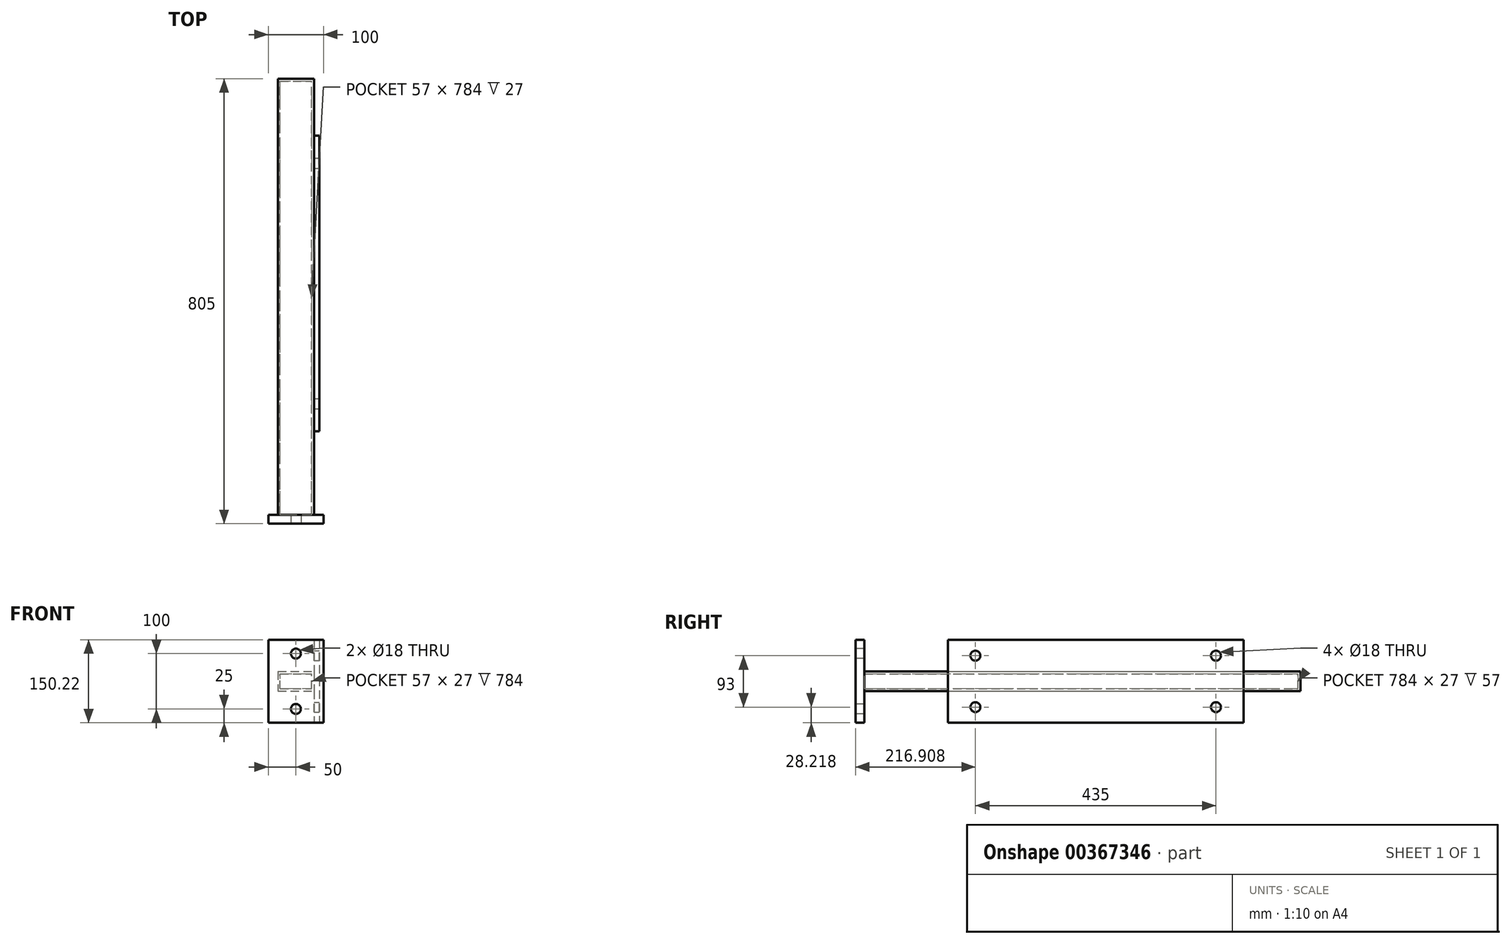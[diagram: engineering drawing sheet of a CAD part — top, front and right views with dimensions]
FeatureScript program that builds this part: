
annotation { "Feature Type Name" : "Feature", "Feature Type Description" : "" }
export const myFeature = defineFeature(function(context is Context, id is Id, definition is map)
    precondition{}
    {
        {
            var Q0;
            Q0=qCreatedBy(makeId("Front.planeOp"),FACE);
            var sketch = newSketch(context, id + "F0", { "sketchPlane" : qUnion([Q0])});
            skLineSegment(sketch, "E0.bottom", {"start": v(-32.5, 17.5) * mm, "end": v(32.5, 17.5) * mm});
            skLineSegment(sketch, "E0.top", {"start": v(-32.5, -17.5) * mm, "end": v(32.5, -17.5) * mm});
            skLineSegment(sketch, "E0.left", {"start": v(-32.5, 17.5) * mm, "end": v(-32.5, -17.5) * mm});
            skLineSegment(sketch, "E0.right", {"start": v(32.5, 17.5) * mm, "end": v(32.5, -17.5) * mm});
            skPoint(sketch, "E0.middle", {"position": v(0, 0) * mm});
            skLineSegment(sketch, "E1.bottom", {"start": v(-28.5, -13.5) * mm, "end": v(28.5, -13.5) * mm});
            skLineSegment(sketch, "E1.top", {"start": v(-28.5, 13.5) * mm, "end": v(28.5, 13.5) * mm});
            skLineSegment(sketch, "E1.left", {"start": v(-28.5, -13.5) * mm, "end": v(-28.5, 13.5) * mm});
            skLineSegment(sketch, "E1.right", {"start": v(28.5, -13.5) * mm, "end": v(28.5, 13.5) * mm});
            skSolve(sketch);
        }
        {
            var Q0;
            Q0 = qSketchRegion(id + "F0", true);
            extrude(context, id + "F1", {"entities" : qUnion([Q0]), "depth" : 784 * mm});
        }
        {
            var Q0;
            Q0=makeQuery(id+"F1.opExtrude","CAP_FACE",FACE,{"disambiguationData":[OSD([sQuery(id+"F0.wireOp",EDGE,"E0.bottom"),sQuery(id+"F0.wireOp",EDGE,"E0.top"),sQuery(id+"F0.wireOp",EDGE,"E0.left"),sQuery(id+"F0.wireOp",EDGE,"E0.right"),sQuery(id+"F0.wireOp",EDGE,"E1.bottom"),sQuery(id+"F0.wireOp",EDGE,"E1.top"),sQuery(id+"F0.wireOp",EDGE,"E1.left"),sQuery(id+"F0.wireOp",EDGE,"E1.right")])],"isStart":false});
            var sketch = newSketch(context, id + "F2", { "sketchPlane" : qUnion([Q0])});
            skLineSegment(sketch, "E2.bottom", {"start": v(-50, -75) * mm, "end": v(50, -75) * mm});
            skLineSegment(sketch, "E2.top", {"start": v(-50, 75) * mm, "end": v(50, 75) * mm});
            skLineSegment(sketch, "E2.left", {"start": v(-50, -75) * mm, "end": v(-50, 75) * mm});
            skLineSegment(sketch, "E2.right", {"start": v(50, -75) * mm, "end": v(50, 75) * mm});
            skPoint(sketch, "E2.middle", {"position": v(0, 0) * mm});
            skSolve(sketch);
        }
        {
            var Q0;
            Q0 = qSketchRegion(id + "F2", true);
            extrude(context, id + "F3", {"entities" : qUnion([Q0]), "operationType" : NewBodyOperationType.ADD, "depth" : 16 * mm});
        }
        {
            var Q0;
            Q0=makeQuery(id+"F3.opExtrude","CAP_FACE",FACE,{"disambiguationData":[OSD([sQuery(id+"F2.wireOp",EDGE,"E2.bottom"),sQuery(id+"F2.wireOp",EDGE,"E2.top"),sQuery(id+"F2.wireOp",EDGE,"E2.left"),sQuery(id+"F2.wireOp",EDGE,"E2.right")])],"isStart":false});
            var sketch = newSketch(context, id + "F4", { "sketchPlane" : qUnion([Q0])});
            skLineSegment(sketch, "E3", {"start": v(0, 75) * mm, "end": v(0, 50) * mm});
            skPoint(sketch, "E3.endSnap0", {"position": v(0, 75) * mm});
            skLineSegment(sketch, "E4", {"start": v(0, -75) * mm, "end": v(0, -50) * mm});
            skPoint(sketch, "E4.endSnap0", {"position": v(0, -75) * mm});
            skSolve(sketch);
        }
        {
            var Q0;
            Q0=sQuery(id+"F4.wireOp",VERTEX,"E3.end");
            var Q1;
            Q1=sQuery(id+"F4.wireOp",VERTEX,"E4.end");
            var Q2;
            Q2=makeQuery(id+"F1.opExtrude","SWEPT_BODY",BODY,{"disambiguationData":[OSD([sQuery(id+"F0.wireOp",EDGE,"E0.bottom"),sQuery(id+"F0.wireOp",EDGE,"E0.top"),sQuery(id+"F0.wireOp",EDGE,"E0.left"),sQuery(id+"F0.wireOp",EDGE,"E0.right"),sQuery(id+"F0.wireOp",EDGE,"E1.bottom"),sQuery(id+"F0.wireOp",EDGE,"E1.top"),sQuery(id+"F0.wireOp",EDGE,"E1.left"),sQuery(id+"F0.wireOp",EDGE,"E1.right")])]});
            hole(context, id + "F5", {"style" : HoleStyle.SIMPLE, "endStyle" : HoleEndStyle.THROUGH, "holeDiameter" : 18 * mm, "isTappedThrough" : true, "tappedDepth" : 12 * mm, "tapClearance" : 3, "locations" : qUnion([Q0, Q1]), "scope" : qUnion([Q2])});
        }
        {
            var Q0;
            Q0=makeQuery(id+"F1.opExtrude","SWEPT_FACE",FACE,{"disambiguationData":[OSD([sQuery(id+"F0.wireOp",EDGE,"E0.right")])]});
            var sketch = newSketch(context, id + "F6", { "sketchPlane" : qUnion([Q0])});
            skLineSegment(sketch, "E5.bottom", {"start": v(-633.1, 75.22) * mm, "end": v(-98.1, 75.22) * mm});
            skLineSegment(sketch, "E5.top", {"start": v(-633.1, -74.78) * mm, "end": v(-98.1, -74.78) * mm});
            skLineSegment(sketch, "E5.left", {"start": v(-633.1, 75.22) * mm, "end": v(-633.1, -74.78) * mm});
            skLineSegment(sketch, "E5.right", {"start": v(-98.1, 75.22) * mm, "end": v(-98.1, -74.78) * mm});
            skSolve(sketch);
        }
        {
            var Q0;
            Q0 = qSketchRegion(id + "F6", true);
            extrude(context, id + "F7", {"entities" : qUnion([Q0]), "operationType" : NewBodyOperationType.ADD, "depth" : 10 * mm});
        }
        {
            var Q0;
            Q0=makeQuery(id+"F7.opExtrude","CAP_FACE",FACE,{"disambiguationData":[OSD([sQuery(id+"F6.wireOp",EDGE,"E5.bottom"),sQuery(id+"F6.wireOp",EDGE,"E5.top"),sQuery(id+"F6.wireOp",EDGE,"E5.left"),sQuery(id+"F6.wireOp",EDGE,"E5.right")])],"isStart":false});
            var sketch = newSketch(context, id + "F8", { "sketchPlane" : qUnion([Q0])});
            skLineSegment(sketch, "E6", {"start": v(-98.1, 75.22) * mm, "end": v(-98.1, 46.22) * mm});
            skLineSegment(sketch, "E7", {"start": v(-98.1, 46.22) * mm, "end": v(-148.1, 46.22) * mm});
            skLineSegment(sketch, "E8", {"start": v(-148.1, 46.22) * mm, "end": v(-148.1, -46.78) * mm});
            skLineSegment(sketch, "E9", {"start": v(-148.1, -46.78) * mm, "end": v(-583.1, -46.78) * mm});
            skLineSegment(sketch, "E10", {"start": v(-583.1, -46.78) * mm, "end": v(-583.1, 46.22) * mm});
            skSolve(sketch);
        }
        {
            var Q0;
            Q0=sQuery(id+"F8.wireOp",VERTEX,"E7.end");
            var Q1;
            Q1=sQuery(id+"F8.wireOp",VERTEX,"E9.start");
            var Q2;
            Q2=sQuery(id+"F8.wireOp",VERTEX,"E10.start");
            var Q3;
            Q3=sQuery(id+"F8.wireOp",VERTEX,"E10.end");
            var Q4;
            Q4=makeQuery(id+"F1.opExtrude","SWEPT_BODY",BODY,{"disambiguationData":[OSD([sQuery(id+"F0.wireOp",EDGE,"E0.bottom"),sQuery(id+"F0.wireOp",EDGE,"E0.top"),sQuery(id+"F0.wireOp",EDGE,"E0.left"),sQuery(id+"F0.wireOp",EDGE,"E0.right"),sQuery(id+"F0.wireOp",EDGE,"E1.bottom"),sQuery(id+"F0.wireOp",EDGE,"E1.top"),sQuery(id+"F0.wireOp",EDGE,"E1.left"),sQuery(id+"F0.wireOp",EDGE,"E1.right")])]});
            hole(context, id + "F9", {"style" : HoleStyle.SIMPLE, "endStyle" : HoleEndStyle.THROUGH, "holeDiameter" : 18 * mm, "isTappedThrough" : true, "tappedDepth" : 12 * mm, "tapClearance" : 3, "locations" : qUnion([Q0, Q1, Q2, Q3]), "scope" : qUnion([Q4])});
        }
        {
            var Q0;
            Q0=makeQuery(id+"F1.opExtrude","CAP_FACE",FACE,{"disambiguationData":[OSD([sQuery(id+"F0.wireOp",EDGE,"E0.bottom"),sQuery(id+"F0.wireOp",EDGE,"E0.top"),sQuery(id+"F0.wireOp",EDGE,"E0.left"),sQuery(id+"F0.wireOp",EDGE,"E0.right"),sQuery(id+"F0.wireOp",EDGE,"E1.bottom"),sQuery(id+"F0.wireOp",EDGE,"E1.top"),sQuery(id+"F0.wireOp",EDGE,"E1.left"),sQuery(id+"F0.wireOp",EDGE,"E1.right")])],"isStart":true});
            var sketch = newSketch(context, id + "F10", { "sketchPlane" : qUnion([Q0])});
            skLineSegment(sketch, "E11.bottom", {"start": v(-32.5, 17.5) * mm, "end": v(32.5, 17.5) * mm});
            skLineSegment(sketch, "E11.top", {"start": v(-32.5, -17.5) * mm, "end": v(32.5, -17.5) * mm});
            skLineSegment(sketch, "E11.left", {"start": v(-32.5, 17.5) * mm, "end": v(-32.5, -17.5) * mm});
            skLineSegment(sketch, "E11.right", {"start": v(32.5, 17.5) * mm, "end": v(32.5, -17.5) * mm});
            skSolve(sketch);
        }
        {
            var Q0;
            Q0 = qSketchRegion(id + "F10", true);
            extrude(context, id + "F11", {"entities" : qUnion([Q0]), "operationType" : NewBodyOperationType.ADD, "depth" : 5 * mm});
        }
    });
